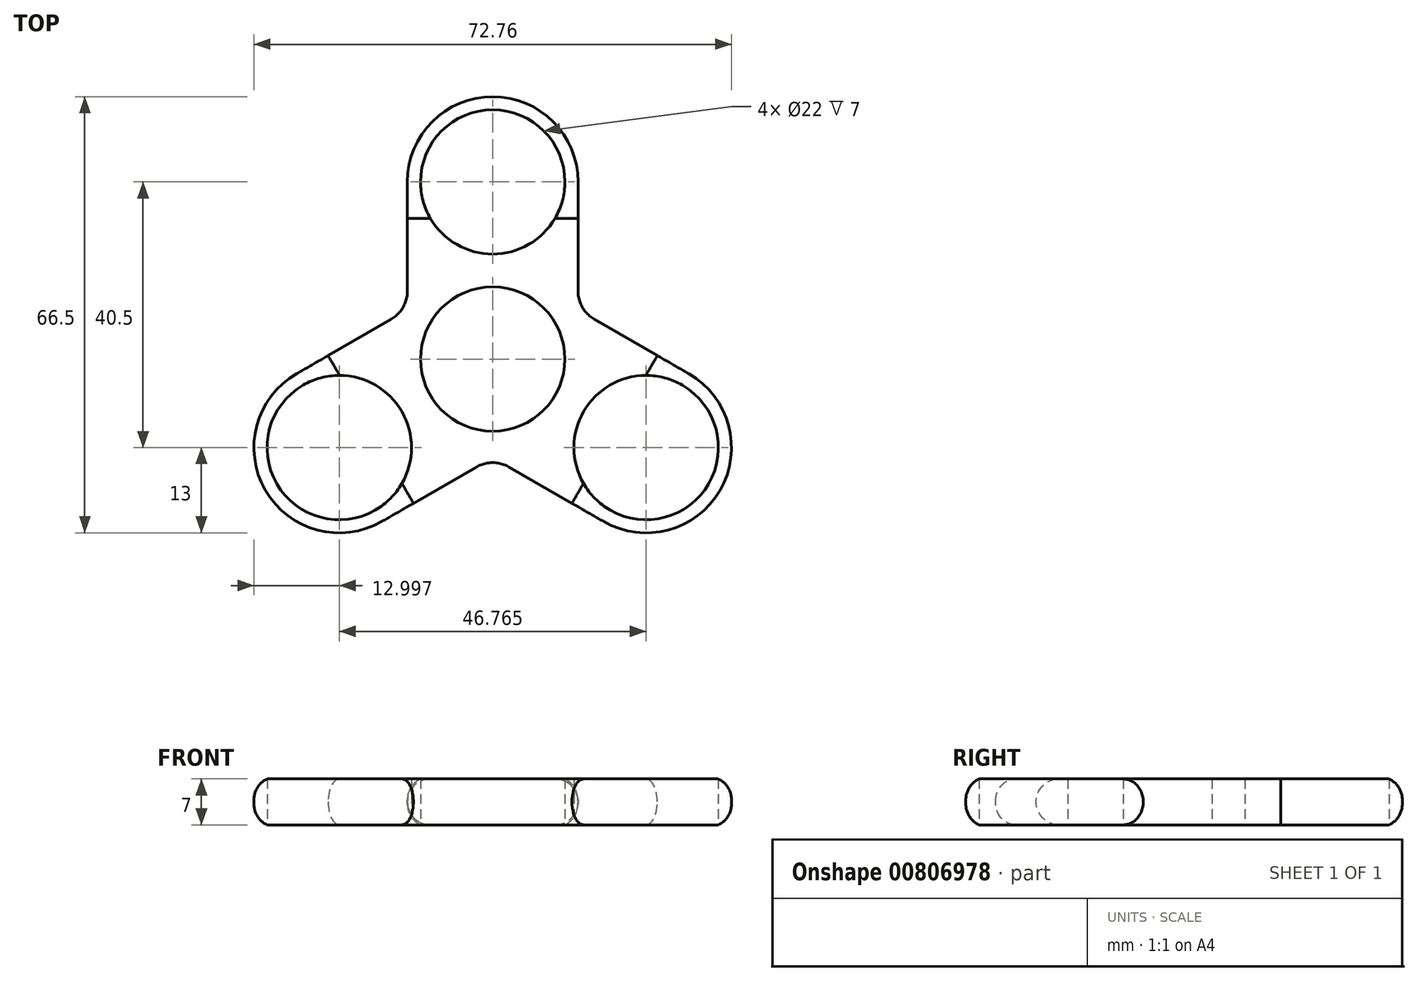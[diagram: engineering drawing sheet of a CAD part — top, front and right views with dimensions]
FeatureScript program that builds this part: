
annotation { "Feature Type Name" : "Feature", "Feature Type Description" : "" }
export const myFeature = defineFeature(function(context is Context, id is Id, definition is map)
    precondition{}
    {
        {
            var Q0;
            Q0=qCreatedBy(makeId("Top.planeOp"),FACE);
            var sketch = newSketch(context, id + "F0", { "sketchPlane" : qUnion([Q0])});
            skCircle(sketch, "E0", {"center": v(0, 0) * mm, "radius": 13 * mm});
            skLineSegment(sketch, "E1.bottom", {"start": v(-13, 0) * mm, "end": v(13, 0) * mm});
            skLineSegment(sketch, "E1.top", {"start": v(-13, 27) * mm, "end": v(13, 27) * mm});
            skLineSegment(sketch, "E1.left", {"start": v(-13, 0) * mm, "end": v(-13, 27) * mm});
            skLineSegment(sketch, "E1.right", {"start": v(13, 0) * mm, "end": v(13, 27) * mm});
            skCircle(sketch, "E2", {"center": v(0, 27) * mm, "radius": 13 * mm});
            skCircle(sketch, "E3", {"center": v(0, 0) * mm, "radius": 11 * mm});
            skCircle(sketch, "E4", {"center": v(0, 27) * mm, "radius": 11 * mm});
            skSolve(sketch);
        }
        {
            var Q0;
            {var subQ0=sQuery(id+"F0.wireOp",EDGE,"E1.bottom");var subQ4=sQuery(id+"F0.wireOp",EDGE,"E3");var subQ5=makeQuery(id+"F0.imprint","INTERSECT",VERTEX,{"disambiguationData":[OD(0.0)],"derivedFrom":[subQ0,subQ4]});Q0=makeQuery(id+"F0.imprint","IMPRINT",FACE,{"disambiguationData":[TD([[makeQuery(id+"F0.imprint","IMPRINT",EDGE,{"disambiguationData":[TD([[subQ5,-1.0]])],"derivedFrom":subQ4}),-1.0]])]});}
            var Q1;
            {var subQ1=sQuery(id+"F0.wireOp",EDGE,"E1.top");var subQ3=sQuery(id+"F0.wireOp",EDGE,"E4");var subQ4=makeQuery(id+"F0.imprint","INTERSECT",VERTEX,{"disambiguationData":[OD(0.0)],"derivedFrom":[subQ1,subQ3]});Q1=makeQuery(id+"F0.imprint","IMPRINT",FACE,{"disambiguationData":[TD([[makeQuery(id+"F0.imprint","IMPRINT",EDGE,{"disambiguationData":[TD([[subQ4,1.0]])],"derivedFrom":subQ3}),-1.0]])]});}
            var Q2;
            {var subQ1=sQuery(id+"F0.wireOp",EDGE,"E1.top");var subQ3=sQuery(id+"F0.wireOp",EDGE,"E4");var subQ4=makeQuery(id+"F0.imprint","INTERSECT",VERTEX,{"disambiguationData":[OD(0.0)],"derivedFrom":[subQ1,subQ3]});Q2=makeQuery(id+"F0.imprint","IMPRINT",FACE,{"disambiguationData":[TD([[makeQuery(id+"F0.imprint","IMPRINT",EDGE,{"disambiguationData":[TD([[subQ4,-1.0]])],"derivedFrom":subQ3}),-1.0]])]});}
            var Q3;
            {var subQ0=sQuery(id+"F0.wireOp",EDGE,"E1.bottom");var subQ4=sQuery(id+"F0.wireOp",EDGE,"E3");var subQ5=makeQuery(id+"F0.imprint","INTERSECT",VERTEX,{"disambiguationData":[OD(0.0)],"derivedFrom":[subQ0,subQ4]});Q3=makeQuery(id+"F0.imprint","IMPRINT",FACE,{"disambiguationData":[TD([[makeQuery(id+"F0.imprint","IMPRINT",EDGE,{"disambiguationData":[TD([[subQ5,1.0]])],"derivedFrom":subQ4}),-1.0]])]});}
            var Q4;
            {var subQ0=sQuery(id+"F0.wireOp",EDGE,"E1.left");Q4=makeQuery(id+"F0.imprint","IMPRINT",FACE,{"disambiguationData":[TD([[makeQuery(id+"F0.imprint","IMPRINT",EDGE,{"derivedFrom":subQ0}),-1.0]])]});}
            extrude(context, id + "F1", {"entities" : qUnion([Q0, Q1, Q2, Q3, Q4]), "depth" : 7 * mm, "offsetDistance" : 25 * mm});
        }
        {
            var Q0;
            Q0=makeQuery(id+"F1.opExtrude","SWEPT_BODY",BODY,{"disambiguationData":[OSD([sQuery(id+"F0.wireOp",EDGE,"E0"),sQuery(id+"F0.wireOp",EDGE,"E1.left"),sQuery(id+"F0.wireOp",EDGE,"E1.right"),sQuery(id+"F0.wireOp",EDGE,"E2"),sQuery(id+"F0.wireOp",EDGE,"E3"),sQuery(id+"F0.wireOp",EDGE,"E4")])]});
            var Q1;
            Q1=makeQuery(id+"F1.opExtrude","SWEPT_FACE",FACE,{"disambiguationData":[OSD([sQuery(id+"F0.wireOp",EDGE,"E3")])]});
            circularPattern(context, id + "F2", {"operationType" : NewBodyOperationType.ADD, "entities" : qUnion([Q0]), "axis" : qUnion([Q1]), "angle" : 360 * degree, "instanceCount" : 3, "equalSpace" : true, "isCentered" : true});
        }
        {
            var Q0;
            Q0=makeQuery(id+"F2.boolean.opBoolean","INTERSECT",EDGE,{"derivedFrom":[makeQuery(id+"F1.opExtrude","SWEPT_FACE",FACE,{"disambiguationData":[OSD([sQuery(id+"F0.wireOp",EDGE,"E1.right")])]}),makeQuery(id+"F2.opPattern","COPY",FACE,{"derivedFrom":makeQuery(id+"F1.opExtrude","SWEPT_FACE",FACE,{"disambiguationData":[OSD([sQuery(id+"F0.wireOp",EDGE,"E1.left")])]}),"instanceName":"-1"})]});
            var Q1;
            Q1=makeQuery(id+"F2.boolean.opBoolean","INTERSECT",EDGE,{"derivedFrom":[makeQuery(id+"F1.opExtrude","SWEPT_FACE",FACE,{"disambiguationData":[OSD([sQuery(id+"F0.wireOp",EDGE,"E1.left")])]}),makeQuery(id+"F2.opPattern","COPY",FACE,{"derivedFrom":makeQuery(id+"F1.opExtrude","SWEPT_FACE",FACE,{"disambiguationData":[OSD([sQuery(id+"F0.wireOp",EDGE,"E1.right")])]}),"instanceName":"-2"})]});
            var Q2;
            {var subQ0=makeQuery(id+"F1.opExtrude","SWEPT_FACE",FACE,{"disambiguationData":[OSD([sQuery(id+"F0.wireOp",EDGE,"E1.right")])]});var subQ1=makeQuery(id+"F1.opExtrude","SWEPT_FACE",FACE,{"disambiguationData":[OSD([sQuery(id+"F0.wireOp",EDGE,"E1.left")])]});Q2=makeQuery(id+"F2.boolean.opBoolean","INTERSECT",EDGE,{"derivedFrom":[makeQuery(id+"F2.opPattern","COPY",FACE,{"derivedFrom":subQ1,"instanceName":"-2"}),makeQuery(id+"F2.opPattern","COPY",FACE,{"derivedFrom":subQ0,"instanceName":"-1"}),makeQuery(id+"F2.opPattern","COPY",FACE,{"derivedFrom":subQ1,"instanceName":"1"}),makeQuery(id+"F2.opPattern","COPY",FACE,{"derivedFrom":subQ0,"instanceName":"2"})]});}
            fillet(context, id + "F3", {"entities" : qUnion([Q0, Q1, Q2]), "radius" : 5 * mm, "tangentPropagation" : true, "allowEdgeOverflow" : false});
        }
        {
            var Q0;
            {var subQ0=sQuery(id+"F0.wireOp",EDGE,"E1.right");var subQ1=sQuery(id+"F0.wireOp",EDGE,"E1.left");var subQ2=makeQuery(id+"F1.opExtrude","CAP_FACE",FACE,{"disambiguationData":[OSD([sQuery(id+"F0.wireOp",EDGE,"E0"),subQ1,subQ0,sQuery(id+"F0.wireOp",EDGE,"E2"),sQuery(id+"F0.wireOp",EDGE,"E3"),sQuery(id+"F0.wireOp",EDGE,"E4")])],"isStart":false});var subQ3=makeQuery(id+"F1.opExtrude","SWEPT_FACE",FACE,{"disambiguationData":[OSD([subQ0])]});var subQ4=makeQuery(id+"F1.opExtrude","SWEPT_FACE",FACE,{"disambiguationData":[OSD([subQ1])]});Q0=makeQuery(id+"F3.opFillet","BLEND_EDGE",EDGE,{"blendedFrom":[makeQuery(id+"F2.boolean.opBoolean","INTERSECT",EDGE,{"derivedFrom":[makeQuery(id+"F2.opPattern","COPY",FACE,{"derivedFrom":subQ4,"instanceName":"-2"}),makeQuery(id+"F2.opPattern","COPY",FACE,{"derivedFrom":subQ3,"instanceName":"-1"}),makeQuery(id+"F2.opPattern","COPY",FACE,{"derivedFrom":subQ4,"instanceName":"1"}),makeQuery(id+"F2.opPattern","COPY",FACE,{"derivedFrom":subQ3,"instanceName":"2"})]}),makeQuery(id+"F2.boolean.opBoolean","MERGE",FACE,{"derivedFrom":[subQ2,makeQuery(id+"F2.opPattern","COPY",FACE,{"derivedFrom":subQ2,"instanceName":"-2"}),makeQuery(id+"F2.opPattern","COPY",FACE,{"derivedFrom":subQ2,"instanceName":"-1"}),makeQuery(id+"F2.opPattern","COPY",FACE,{"derivedFrom":subQ2,"instanceName":"1"}),makeQuery(id+"F2.opPattern","COPY",FACE,{"derivedFrom":subQ2,"instanceName":"2"})]})],"blendedInto":[makeQuery(id+"F2.boolean.opBoolean","MERGE",FACE,{"derivedFrom":[subQ2,makeQuery(id+"F2.opPattern","COPY",FACE,{"derivedFrom":subQ2,"instanceName":"-2"}),makeQuery(id+"F2.opPattern","COPY",FACE,{"derivedFrom":subQ2,"instanceName":"-1"}),makeQuery(id+"F2.opPattern","COPY",FACE,{"derivedFrom":subQ2,"instanceName":"1"}),makeQuery(id+"F2.opPattern","COPY",FACE,{"derivedFrom":subQ2,"instanceName":"2"})]})]});}
            var Q1;
            {var subQ0=sQuery(id+"F0.wireOp",EDGE,"E1.right");var subQ1=sQuery(id+"F0.wireOp",EDGE,"E1.left");var subQ2=makeQuery(id+"F1.opExtrude","CAP_FACE",FACE,{"disambiguationData":[OSD([sQuery(id+"F0.wireOp",EDGE,"E0"),subQ1,subQ0,sQuery(id+"F0.wireOp",EDGE,"E2"),sQuery(id+"F0.wireOp",EDGE,"E3"),sQuery(id+"F0.wireOp",EDGE,"E4")])],"isStart":true});var subQ3=makeQuery(id+"F1.opExtrude","SWEPT_FACE",FACE,{"disambiguationData":[OSD([subQ0])]});var subQ4=makeQuery(id+"F1.opExtrude","SWEPT_FACE",FACE,{"disambiguationData":[OSD([subQ1])]});Q1=makeQuery(id+"F3.opFillet","BLEND_EDGE",EDGE,{"blendedFrom":[makeQuery(id+"F2.boolean.opBoolean","INTERSECT",EDGE,{"derivedFrom":[makeQuery(id+"F2.opPattern","COPY",FACE,{"derivedFrom":subQ4,"instanceName":"-2"}),makeQuery(id+"F2.opPattern","COPY",FACE,{"derivedFrom":subQ3,"instanceName":"-1"}),makeQuery(id+"F2.opPattern","COPY",FACE,{"derivedFrom":subQ4,"instanceName":"1"}),makeQuery(id+"F2.opPattern","COPY",FACE,{"derivedFrom":subQ3,"instanceName":"2"})]}),makeQuery(id+"F2.boolean.opBoolean","MERGE",FACE,{"derivedFrom":[subQ2,makeQuery(id+"F2.opPattern","COPY",FACE,{"derivedFrom":subQ2,"instanceName":"-2"}),makeQuery(id+"F2.opPattern","COPY",FACE,{"derivedFrom":subQ2,"instanceName":"-1"}),makeQuery(id+"F2.opPattern","COPY",FACE,{"derivedFrom":subQ2,"instanceName":"1"}),makeQuery(id+"F2.opPattern","COPY",FACE,{"derivedFrom":subQ2,"instanceName":"2"})]})],"blendedInto":[makeQuery(id+"F2.boolean.opBoolean","MERGE",FACE,{"derivedFrom":[subQ2,makeQuery(id+"F2.opPattern","COPY",FACE,{"derivedFrom":subQ2,"instanceName":"-2"}),makeQuery(id+"F2.opPattern","COPY",FACE,{"derivedFrom":subQ2,"instanceName":"-1"}),makeQuery(id+"F2.opPattern","COPY",FACE,{"derivedFrom":subQ2,"instanceName":"1"}),makeQuery(id+"F2.opPattern","COPY",FACE,{"derivedFrom":subQ2,"instanceName":"2"})]})]});}
            fillet(context, id + "F4", {"entities" : qUnion([Q0, Q1]), "radius" : 3.5 * mm, "tangentPropagation" : true, "allowEdgeOverflow" : false});
        }
    });
